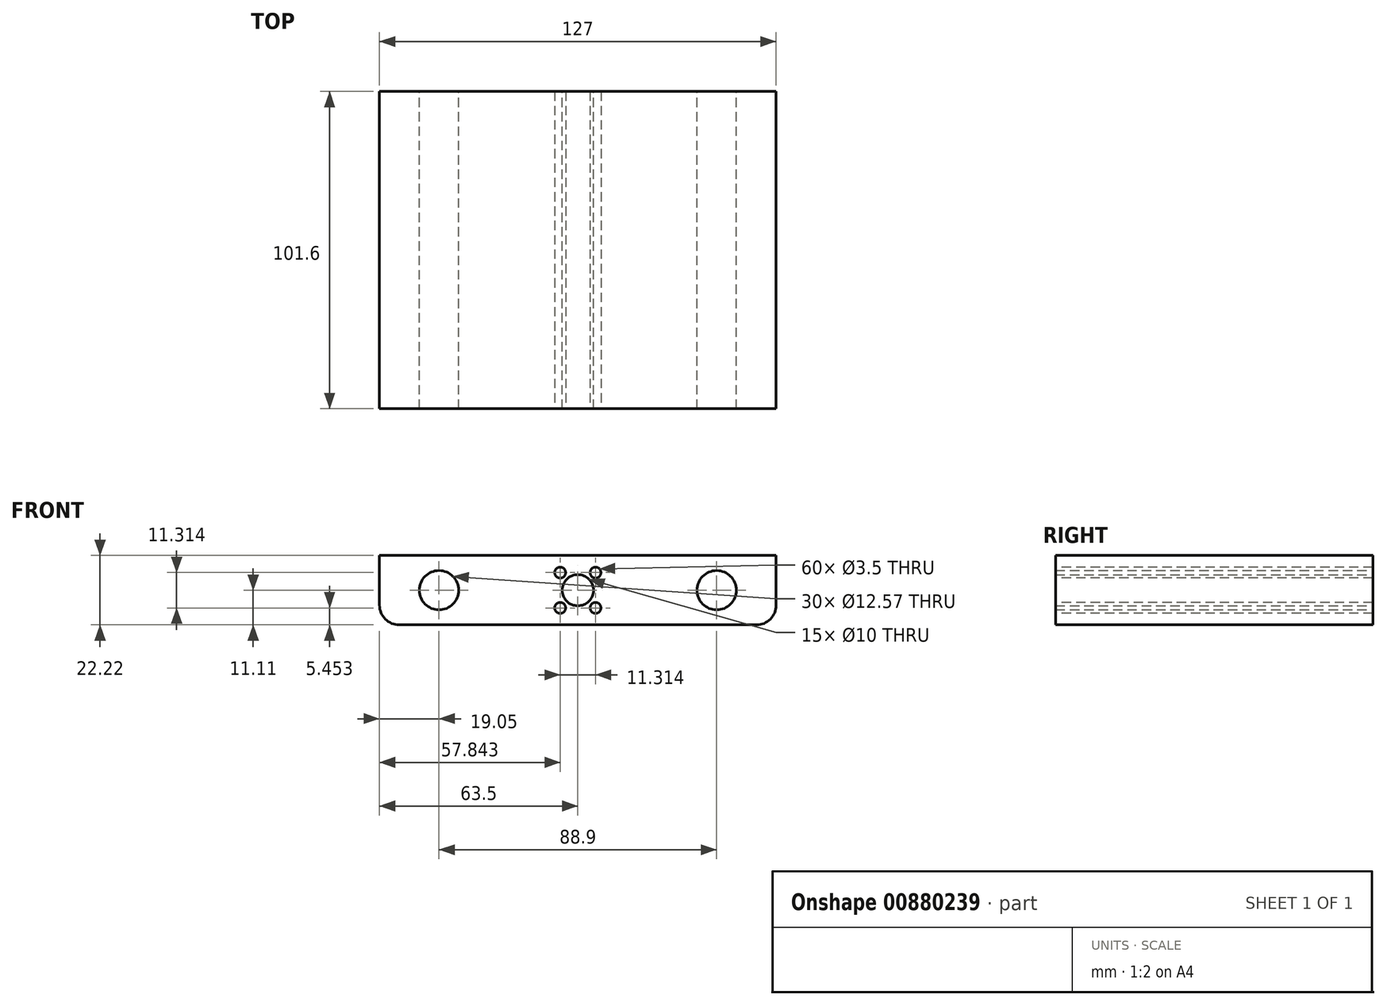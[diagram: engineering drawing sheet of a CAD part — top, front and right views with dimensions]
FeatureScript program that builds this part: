
annotation { "Feature Type Name" : "Feature", "Feature Type Description" : "" }
export const myFeature = defineFeature(function(context is Context, id is Id, definition is map)
    precondition{}
    {
        {
            var Q0;
            Q0=qCreatedBy(makeId("Front.planeOp"),FACE);
            var sketch = newSketch(context, id + "F0", { "sketchPlane" : qUnion([Q0])});
            skCircle(sketch, "E0", {"center": v(0, 0) * mm, "radius": 5 * mm});
            skCircle(sketch, "E1", {"center": v(44.45, 0) * mm, "radius": 6.29 * mm});
            skCircle(sketch, "E2", {"center": v(-44.45, 0) * mm, "radius": 6.29 * mm});
            skLineSegment(sketch, "E3", {"start": v(-44.45, 0) * mm, "end": v(0, 0) * mm, "construction": true});
            skLineSegment(sketch, "E4", {"start": v(44.45, 0) * mm, "end": v(0, 0) * mm, "construction": true});
            skLineSegment(sketch, "E5.bottom", {"start": v(-63.5, 11.11) * mm, "end": v(63.5, 11.11) * mm});
            skLineSegment(sketch, "E5.top", {"start": v(-63.5, -11.11) * mm, "end": v(63.5, -11.11) * mm});
            skLineSegment(sketch, "E5.left", {"start": v(-63.5, 11.11) * mm, "end": v(-63.5, -11.11) * mm});
            skLineSegment(sketch, "E5.right", {"start": v(63.5, 11.11) * mm, "end": v(63.5, -11.11) * mm});
            skSolve(sketch);
        }
        {
            var Q0;
            Q0=qSketchRegion(id+"F0",true);
            extrude(context, id + "F1", {"entities" : qUnion([Q0]), "depth" : 101.6 * mm});
        }
        {
            var Q0;
            Q0=makeQuery(id+"F1.opExtrude","SWEPT_EDGE",EDGE,{"disambiguationData":[OSD([sQuery(id+"F0.wireOp",EDGE,"E5.top"),sQuery(id+"F0.wireOp",EDGE,"E5.left")])]});
            var Q1;
            Q1=makeQuery(id+"F1.opExtrude","SWEPT_EDGE",EDGE,{"disambiguationData":[OSD([sQuery(id+"F0.wireOp",EDGE,"E5.top"),sQuery(id+"F0.wireOp",EDGE,"E5.right")])]});
            fillet(context, id + "F2", {"entities" : qUnion([Q0, Q1]), "radius" : 6.35 * mm, "tangentPropagation" : true, "allowEdgeOverflow" : false});
        }
        {
            var Q0;
            Q0=makeQuery(id+"F1.opExtrude","CAP_FACE",FACE,{"disambiguationData":[OSD([sQuery(id+"F0.wireOp",EDGE,"E0"),sQuery(id+"F0.wireOp",EDGE,"E1"),sQuery(id+"F0.wireOp",EDGE,"E2"),sQuery(id+"F0.wireOp",EDGE,"E5.bottom"),sQuery(id+"F0.wireOp",EDGE,"E5.top"),sQuery(id+"F0.wireOp",EDGE,"E5.left"),sQuery(id+"F0.wireOp",EDGE,"E5.right")])],"isStart":false});
            var sketch = newSketch(context, id + "F3", { "sketchPlane" : qUnion([Q0])});
            skCircle(sketch, "E6", {"center": v(0, 0) * mm, "radius": 8 * mm, "construction": true});
            skCircle(sketch, "E7", {"center": v(-5.66, 5.66) * mm, "radius": 1.75 * mm});
            skCircle(sketch, "E8", {"center": v(5.66, 5.66) * mm, "radius": 1.75 * mm});
            skCircle(sketch, "E9", {"center": v(5.66, -5.66) * mm, "radius": 1.75 * mm});
            skCircle(sketch, "E10", {"center": v(-5.66, -5.66) * mm, "radius": 1.75 * mm});
            skLineSegment(sketch, "E11", {"start": v(-5.66, -5.66) * mm, "end": v(-5.66, 5.66) * mm, "construction": true});
            skLineSegment(sketch, "E12", {"start": v(5.66, 5.66) * mm, "end": v(-5.66, 5.66) * mm, "construction": true});
            skSolve(sketch);
        }
        {
            var Q0;
            Q0=qSketchRegion(id+"F3",true);
            extrude(context, id + "F4", {"entities" : qUnion([Q0]), "operationType" : NewBodyOperationType.REMOVE, "endBound" : BoundingType.THROUGH_ALL, "oppositeDirection" : true, "depth" : 25.4 * mm});
        }
    });
